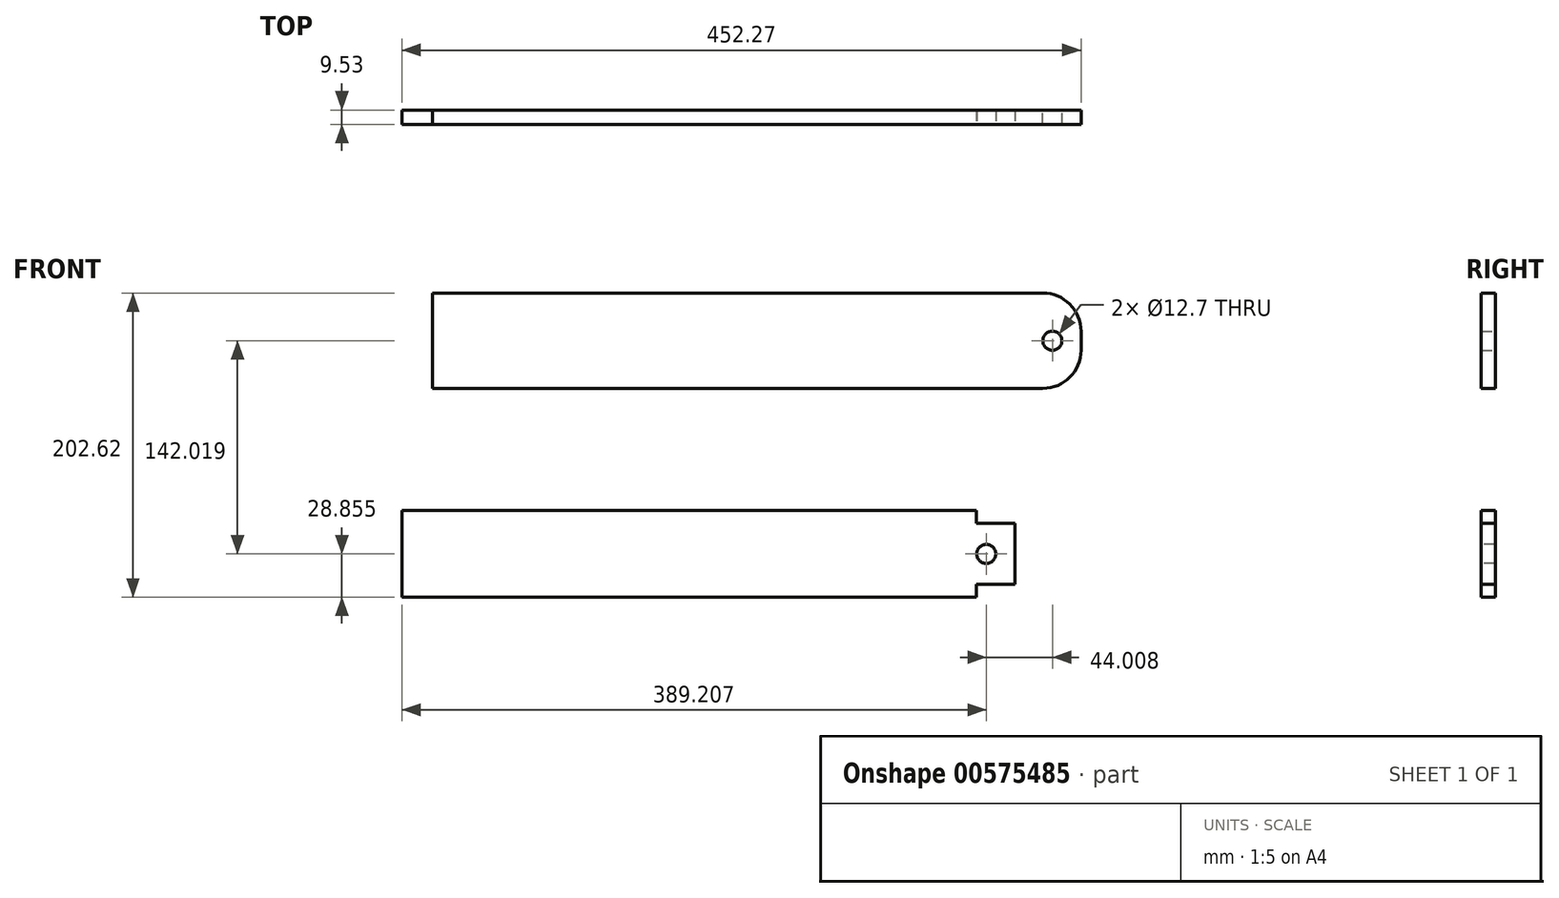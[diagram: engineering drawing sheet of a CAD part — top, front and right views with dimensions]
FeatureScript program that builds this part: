
annotation { "Feature Type Name" : "Feature", "Feature Type Description" : "" }
export const myFeature = defineFeature(function(context is Context, id is Id, definition is map)
    precondition{}
    {
        {
            var Q0;
            Q0=qCreatedBy(makeId("Front.planeOp"),FACE);
            var sketch = newSketch(context, id + "F0", { "sketchPlane" : qUnion([Q0])});
            skLineSegment(sketch, "E0.bottom", {"start": v(-191.17, 3.95) * mm, "end": v(217.09, 3.95) * mm});
            skLineSegment(sketch, "E0.top", {"start": v(-191.17, -53.76) * mm, "end": v(217.09, -53.76) * mm});
            skLineSegment(sketch, "E0.left", {"start": v(-191.17, 3.95) * mm, "end": v(-191.17, -53.76) * mm});
            skLineSegment(sketch, "E0.right", {"start": v(217.09, 3.95) * mm, "end": v(217.09, -53.76) * mm});
            skSolve(sketch);
        }
        {
            var Q0;
            Q0=makeQuery(id+"F0.imprint","IMPRINT",FACE,{"disambiguationData":[TD([[makeQuery(id+"F0.imprint","IMPRINT",EDGE,{"derivedFrom":sQuery(id+"F0.wireOp",EDGE,"E0.bottom")}),-1.0]])]});
            extrude(context, id + "F1", {"entities" : qUnion([Q0]), "depth" : 9.52 * mm, "offsetDistance" : 25.4 * mm});
        }
        {
            var Q0;
            Q0=makeQuery(id+"F1.opExtrude","CAP_FACE",FACE,{"disambiguationData":[OSD([sQuery(id+"F0.wireOp",EDGE,"E0.bottom"),sQuery(id+"F0.wireOp",EDGE,"E0.top"),sQuery(id+"F0.wireOp",EDGE,"E0.left"),sQuery(id+"F0.wireOp",EDGE,"E0.right")])],"isStart":false});
            var sketch = newSketch(context, id + "F2", { "sketchPlane" : qUnion([Q0])});
            skCircle(sketch, "E1", {"center": v(198.04, -24.9) * mm, "radius": 6.35 * mm});
            skSolve(sketch);
        }
        {
            var Q0;
            Q0=makeQuery(id+"F2.imprint","IMPRINT",FACE,{"disambiguationData":[TD([[makeQuery(id+"F2.imprint","IMPRINT",EDGE,{"derivedFrom":sQuery(id+"F2.wireOp",EDGE,"E1")}),1.0]])]});
            extrude(context, id + "F3", {"entities" : qUnion([Q0]), "operationType" : NewBodyOperationType.REMOVE, "oppositeDirection" : true, "depth" : 9.52 * mm, "offsetDistance" : 25.4 * mm});
        }
        {
            var Q0;
            Q0=makeQuery(id+"F1.opExtrude","CAP_FACE",FACE,{"disambiguationData":[OSD([sQuery(id+"F0.wireOp",EDGE,"E0.bottom"),sQuery(id+"F0.wireOp",EDGE,"E0.top"),sQuery(id+"F0.wireOp",EDGE,"E0.left"),sQuery(id+"F0.wireOp",EDGE,"E0.right")])],"isStart":false});
            var sketch = newSketch(context, id + "F4", { "sketchPlane" : qUnion([Q0])});
            skLineSegment(sketch, "E2.bottom", {"start": v(191.48, 3.95) * mm, "end": v(217.09, 3.95) * mm});
            skLineSegment(sketch, "E2.top", {"start": v(191.48, -4.59) * mm, "end": v(217.09, -4.59) * mm});
            skLineSegment(sketch, "E2.left", {"start": v(191.48, 3.95) * mm, "end": v(191.48, -4.59) * mm});
            skLineSegment(sketch, "E2.right", {"start": v(217.09, 3.95) * mm, "end": v(217.09, -4.59) * mm});
            skLineSegment(sketch, "E3.bottom", {"start": v(191.48, -45.23) * mm, "end": v(217.09, -45.23) * mm});
            skLineSegment(sketch, "E3.top", {"start": v(191.48, -53.76) * mm, "end": v(217.09, -53.76) * mm});
            skLineSegment(sketch, "E3.left", {"start": v(191.48, -45.23) * mm, "end": v(191.48, -53.76) * mm});
            skLineSegment(sketch, "E3.right", {"start": v(217.09, -45.23) * mm, "end": v(217.09, -53.76) * mm});
            skSolve(sketch);
        }
        {
            var Q0;
            Q0=makeQuery(id+"F4.imprint","IMPRINT",FACE,{"disambiguationData":[TD([[makeQuery(id+"F4.imprint","IMPRINT",EDGE,{"derivedFrom":sQuery(id+"F4.wireOp",EDGE,"E2.bottom")}),-1.0]])]});
            extrude(context, id + "F5", {"entities" : qUnion([Q0]), "operationType" : NewBodyOperationType.REMOVE, "oppositeDirection" : true, "depth" : 25.4 * mm, "offsetDistance" : 25.4 * mm});
        }
        {
            var Q0;
            Q0=makeQuery(id+"F4.imprint","IMPRINT",FACE,{"disambiguationData":[TD([[makeQuery(id+"F4.imprint","IMPRINT",EDGE,{"derivedFrom":sQuery(id+"F4.wireOp",EDGE,"E3.bottom")}),-1.0]])]});
            extrude(context, id + "F6", {"entities" : qUnion([Q0]), "operationType" : NewBodyOperationType.REMOVE, "oppositeDirection" : true, "depth" : 25.4 * mm, "offsetDistance" : 25.4 * mm});
        }
        {
            var Q0;
            Q0=qCreatedBy(makeId("Front.planeOp"),FACE);
            var sketch = newSketch(context, id + "F7", { "sketchPlane" : qUnion([Q0])});
            skLineSegment(sketch, "E4.bottom", {"start": v(-170.7, 148.86) * mm, "end": v(235.7, 148.86) * mm});
            skLineSegment(sketch, "E4.top", {"start": v(-170.7, 85.36) * mm, "end": v(235.7, 85.36) * mm});
            skLineSegment(sketch, "E4.left", {"start": v(-170.7, 148.86) * mm, "end": v(-170.7, 85.36) * mm});
            skLineSegment(sketch, "E4.right", {"start": v(261.1, 123.46) * mm, "end": v(261.1, 110.76) * mm});
            skCircle(sketch, "E5", {"center": v(242.05, 117.11) * mm, "radius": 6.35 * mm});
            skPoint(sketch, "E6", {"position": v(261.1, 117.11) * mm});
            skPoint(sketch, "E7.visualSharp", {"position": v(261.1, 148.86) * mm});
            skArc(sketch, "E7.filletArc", {"start": v(261.1, 123.46) * mm, "mid": v(253.66, 141.42) * mm, "end": v(235.7, 148.86) * mm});
            skPoint(sketch, "E8.visualSharp", {"position": v(261.1, 85.36) * mm});
            skArc(sketch, "E8.filletArc", {"start": v(235.7, 85.36) * mm, "mid": v(253.66, 92.8) * mm, "end": v(261.1, 110.76) * mm});
            skSolve(sketch);
        }
        {
            var Q0;
            Q0=makeQuery(id+"F7.imprint","IMPRINT",FACE,{"disambiguationData":[TD([[makeQuery(id+"F7.imprint","IMPRINT",EDGE,{"derivedFrom":sQuery(id+"F7.wireOp",EDGE,"E4.bottom")}),-1.0]])]});
            extrude(context, id + "F8", {"entities" : qUnion([Q0]), "depth" : 9.52 * mm, "offsetDistance" : 25.4 * mm});
        }
    });
